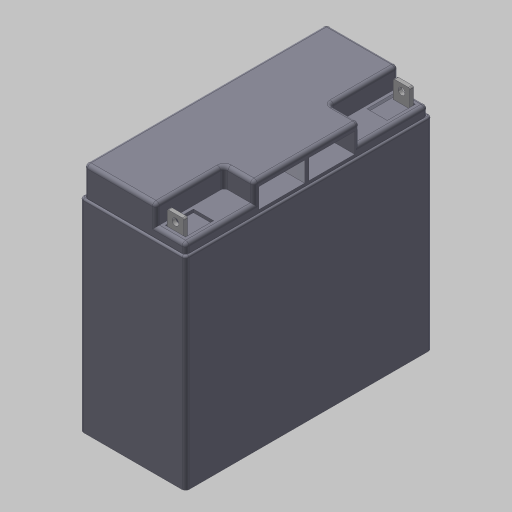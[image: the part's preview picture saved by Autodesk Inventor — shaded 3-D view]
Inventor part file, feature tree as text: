
AUTODESK INVENTOR PART (.ipt)
format: ipt  version: 2023.5 (Build 275446000, 446)  size: 304,128 bytes
history: native  units: mm
features: plane x2, imported_body x1
ambient origin geometry x8: Origin, YZ Plane, XZ Plane, XY Plane, X Axis, Y Axis, Z Axis, Center Point
bodies: Solid1 (feature_tree)
feature tree (3):
  imported_body  "Base1"
  plane  "Work Plane1"
  plane  "Work Plane2"
